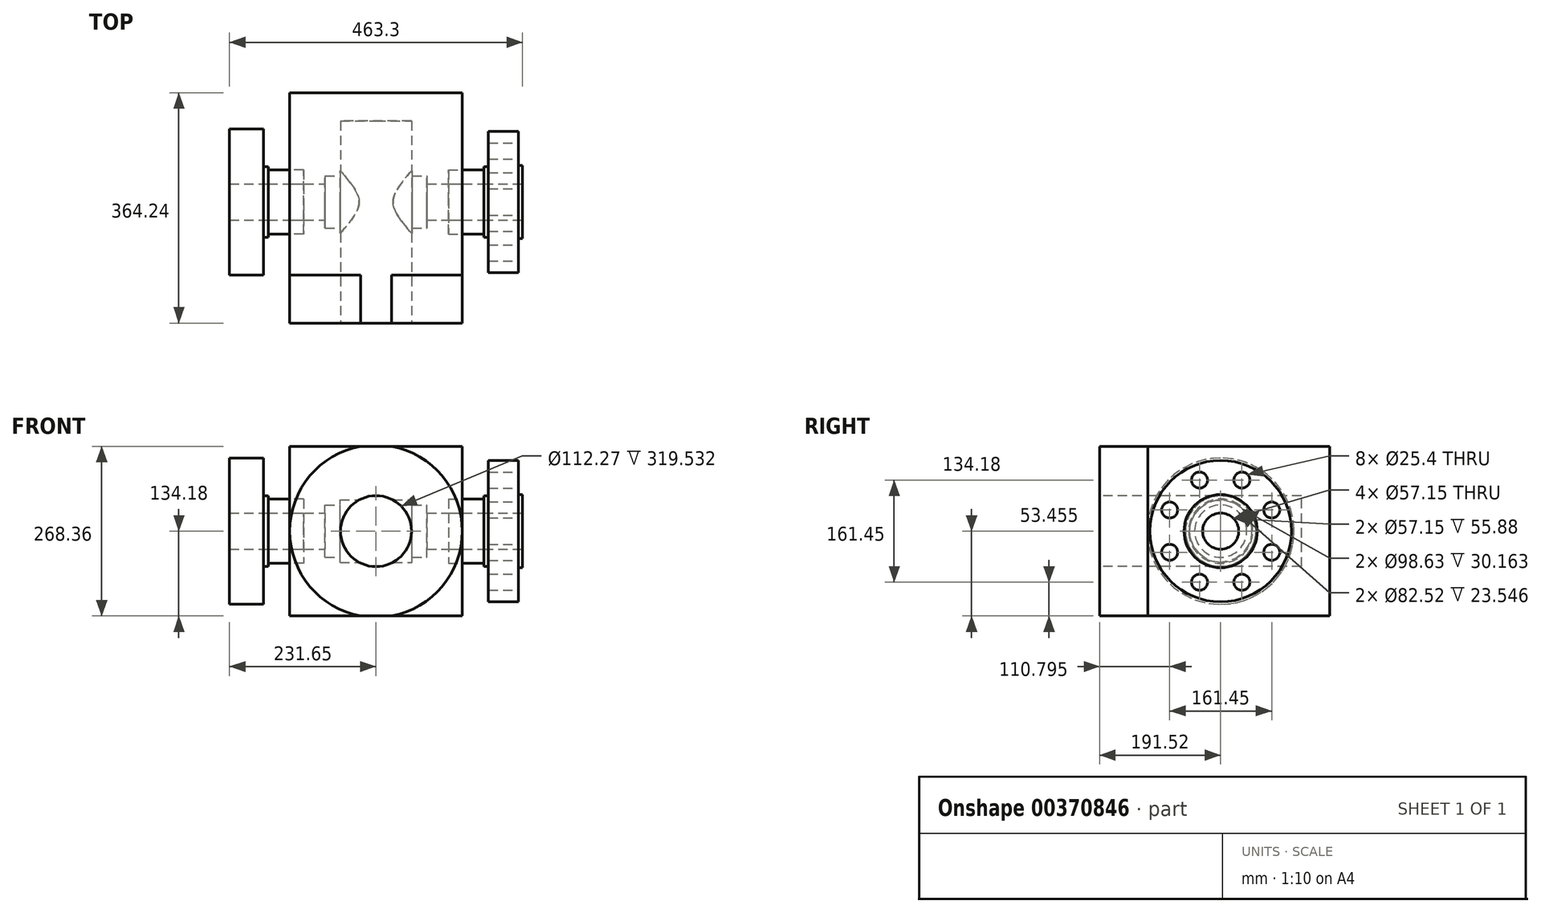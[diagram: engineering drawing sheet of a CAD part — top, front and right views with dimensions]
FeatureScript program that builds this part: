
annotation { "Feature Type Name" : "Feature", "Feature Type Description" : "" }
export const myFeature = defineFeature(function(context is Context, id is Id, definition is map)
    precondition{}
    {
        {
            var Q0;
            Q0=qCreatedBy(makeId("Front.planeOp"),FACE);
            var sketch = newSketch(context, id + "F0", { "sketchPlane" : qUnion([Q0])});
            skLineSegment(sketch, "E0.bottom", {"start": v(-136.4, -134.18) * mm, "end": v(136.4, -134.18) * mm});
            skLineSegment(sketch, "E0.top", {"start": v(-136.4, 134.18) * mm, "end": v(136.4, 134.18) * mm});
            skLineSegment(sketch, "E0.left", {"start": v(-136.4, -134.18) * mm, "end": v(-136.4, 134.18) * mm});
            skLineSegment(sketch, "E0.right", {"start": v(136.4, -134.18) * mm, "end": v(136.4, 134.18) * mm});
            skPoint(sketch, "E0.middle", {"position": v(0, 0) * mm});
            skSolve(sketch);
        }
        {
            var Q0;
            Q0=qSketchRegion(id+"F0",true);
            extrude(context, id + "F1", {"entities" : qUnion([Q0]), "depth" : 191.52 * mm});
        }
        {
            var Q0;
            Q0=makeQuery(id+"F1.opExtrude","CAP_FACE",FACE,{"disambiguationData":[OSD([sQuery(id+"F0.wireOp",EDGE,"E0.bottom"),sQuery(id+"F0.wireOp",EDGE,"E0.top"),sQuery(id+"F0.wireOp",EDGE,"E0.left"),sQuery(id+"F0.wireOp",EDGE,"E0.right")])],"isStart":true});
            extrude(context, id + "F2", {"entities" : qUnion([Q0]), "operationType" : NewBodyOperationType.ADD, "depth" : 172.72 * mm});
        }
        {
            var Q0;
            Q0=qCreatedBy(makeId("Right.planeOp"),FACE);
            cPlane(context, id + "F3", {"entities" : qUnion([Q0]), "cplaneType" : CPlaneType.OFFSET, "offset" : 231.65 * mm, "width" : 152.4 * mm, "height" : 152.4 * mm});
        }
        {
            var Q0;
            Q0=qCreatedBy(id+"F3.planeOp",FACE);
            var sketch = newSketch(context, id + "F4", { "sketchPlane" : qUnion([Q0])});
            skCircle(sketch, "E1", {"center": v(0, 0) * mm, "radius": 115.82 * mm});
            skSolve(sketch);
        }
        {
            var Q0;
            Q0=makeQuery(id+"F4.imprint","IMPRINT",FACE,{"disambiguationData":[TD([[makeQuery(id+"F4.imprint","IMPRINT",EDGE,{"derivedFrom":sQuery(id+"F4.wireOp",EDGE,"E1")}),1.0]])]});
            var Q1;
            Q1=qConstructionFilter(qBodyType(qCreatedBy(id+"F4",EDGE),BodyType.WIRE),ConstructionObject.NO);
            extrude(context, id + "F5", {"entities" : qUnion([Q0]), "surfaceEntities" : qUnion([Q1]), "oppositeDirection" : true, "depth" : 61.2 * mm});
        }
        {
            var Q0;
            Q0=makeQuery(id+"F5.opExtrude","CAP_FACE",FACE,{"disambiguationData":[OSD([sQuery(id+"F4.wireOp",EDGE,"E1")])],"isStart":false});
            var sketch = newSketch(context, id + "F6", { "sketchPlane" : qUnion([Q0])});
            skCircle(sketch, "E2", {"center": v(0, 0) * mm, "radius": 50.8 * mm});
            skSolve(sketch);
        }
        {
            var Q0;
            Q0=qSketchRegion(id+"F6",true);
            extrude(context, id + "F7", {"entities" : qUnion([Q0]), "depth" : 55.88 * mm});
        }
        {
            var Q0;
            Q0=qCreatedBy(makeId("Right.planeOp"),FACE);
            var sketch = newSketch(context, id + "F8", { "sketchPlane" : qUnion([Q0])});
            skLineSegment(sketch, "E3", {"start": v(0, 0) * mm, "end": v(0, 210.58) * mm});
            skSolve(sketch);
        }
        {
            var Q0;
            Q0=makeQuery(id+"F7.opExtrude","SWEPT_BODY",BODY,{"disambiguationData":[OSD([sQuery(id+"F6.wireOp",EDGE,"E2")])]});
            var Q1;
            Q1=makeQuery(id+"F5.opExtrude","SWEPT_BODY",BODY,{"disambiguationData":[OSD([sQuery(id+"F4.wireOp",EDGE,"E1")])]});
            var Q2;
            Q2=sQuery(id+"F8.wireOp",EDGE,"E3");
            circularPattern(context, id + "F9", {"entities" : qUnion([Q0, Q1]), "axis" : qUnion([Q2]), "angle" : 360 * degree, "instanceCount" : 2, "equalSpace" : true});
        }
        {
            var Q0;
            Q0=makeQuery(id+"F5.opExtrude","CAP_FACE",FACE,{"disambiguationData":[OSD([sQuery(id+"F4.wireOp",EDGE,"E1")])],"isStart":true});
            var sketch = newSketch(context, id + "F10", { "sketchPlane" : qUnion([Q0])});
            skCircle(sketch, "E4", {"center": v(0, 0) * mm, "radius": 28.57 * mm});
            skSolve(sketch);
        }
        {
            var Q0;
            Q0=qSketchRegion(id+"F10",true);
            extrude(context, id + "F11", {"entities" : qUnion([Q0]), "operationType" : NewBodyOperationType.REMOVE, "oppositeDirection" : true, "depth" : 701.04 * mm});
        }
        {
            var Q0;
            Q0=makeQuery(id+"F1.opExtrude","CAP_FACE",FACE,{"disambiguationData":[OSD([sQuery(id+"F0.wireOp",EDGE,"E0.bottom"),sQuery(id+"F0.wireOp",EDGE,"E0.top"),sQuery(id+"F0.wireOp",EDGE,"E0.left"),sQuery(id+"F0.wireOp",EDGE,"E0.right")])],"isStart":false});
            var sketch = newSketch(context, id + "F12", { "sketchPlane" : qUnion([Q0])});
            skCircle(sketch, "E5", {"center": v(0, 0) * mm, "radius": 56.13 * mm});
            skSolve(sketch);
        }
        {
            var Q0;
            Q0=qSketchRegion(id+"F12",true);
            extrude(context, id + "F13", {"entities" : qUnion([Q0]), "operationType" : NewBodyOperationType.REMOVE, "oppositeDirection" : true, "depth" : 319.53 * mm});
        }
        {
            var Q0;
            Q0=makeQuery(id+"F1.opExtrude","CAP_FACE",FACE,{"disambiguationData":[OSD([sQuery(id+"F0.wireOp",EDGE,"E0.bottom"),sQuery(id+"F0.wireOp",EDGE,"E0.top"),sQuery(id+"F0.wireOp",EDGE,"E0.left"),sQuery(id+"F0.wireOp",EDGE,"E0.right")])],"isStart":false});
            var sketch = newSketch(context, id + "F14", { "sketchPlane" : qUnion([Q0])});
            skCircle(sketch, "E6", {"center": v(0, 0) * mm, "radius": 136.4 * mm});
            skSolve(sketch);
        }
        {
            var Q0;
            {var subQ0=sQuery(id+"F14.wireOp",EDGE,"E6");var subQ1=makeQuery(id+"F1.opExtrude","CAP_EDGE",EDGE,{"disambiguationData":[OSD([sQuery(id+"F0.wireOp",EDGE,"E0.top")])],"isStart":false});var subQ2=makeQuery(id+"F14.imprint","INTERSECT",VERTEX,{"disambiguationData":[OD(1.0)],"derivedFrom":[subQ1,subQ0]});Q0=makeQuery(id+"F14.imprint","IMPRINT",FACE,{"disambiguationData":[TD([[makeQuery(id+"F14.imprint","IMPRINT",EDGE,{"disambiguationData":[TD([[subQ2,-1.0]])],"derivedFrom":subQ0}),-1.0]])]});}
            var Q1;
            {var subQ0=sQuery(id+"F14.wireOp",EDGE,"E6");var subQ1=makeQuery(id+"F1.opExtrude","CAP_EDGE",EDGE,{"disambiguationData":[OSD([sQuery(id+"F0.wireOp",EDGE,"E0.top")])],"isStart":false});var subQ2=makeQuery(id+"F14.imprint","INTERSECT",VERTEX,{"disambiguationData":[OD(0.0)],"derivedFrom":[subQ1,subQ0]});Q1=makeQuery(id+"F14.imprint","IMPRINT",FACE,{"disambiguationData":[TD([[makeQuery(id+"F14.imprint","IMPRINT",EDGE,{"disambiguationData":[TD([[subQ2,1.0]])],"derivedFrom":subQ0}),-1.0]])]});}
            var Q2;
            {var subQ0=sQuery(id+"F14.wireOp",EDGE,"E6");var subQ1=makeQuery(id+"F1.opExtrude","CAP_EDGE",EDGE,{"disambiguationData":[OSD([sQuery(id+"F0.wireOp",EDGE,"E0.right")])],"isStart":false});var subQ2=makeQuery(id+"F14.imprint","INTERSECT",VERTEX,{"derivedFrom":[subQ1,subQ0]});Q2=makeQuery(id+"F14.imprint","IMPRINT",FACE,{"disambiguationData":[TD([[makeQuery(id+"F14.imprint","IMPRINT",EDGE,{"disambiguationData":[TD([[subQ2,1.0]])],"derivedFrom":subQ0}),-1.0]])]});}
            var Q3;
            {var subQ0=sQuery(id+"F14.wireOp",EDGE,"E6");var subQ1=makeQuery(id+"F1.opExtrude","CAP_EDGE",EDGE,{"disambiguationData":[OSD([sQuery(id+"F0.wireOp",EDGE,"E0.left")])],"isStart":false});var subQ2=makeQuery(id+"F14.imprint","INTERSECT",VERTEX,{"derivedFrom":[subQ1,subQ0]});Q3=makeQuery(id+"F14.imprint","IMPRINT",FACE,{"disambiguationData":[TD([[makeQuery(id+"F14.imprint","IMPRINT",EDGE,{"disambiguationData":[TD([[subQ2,-1.0]])],"derivedFrom":subQ0}),-1.0]])]});}
            extrude(context, id + "F15", {"entities" : qUnion([Q0, Q1, Q2, Q3]), "operationType" : NewBodyOperationType.REMOVE, "oppositeDirection" : true, "depth" : 76.2 * mm});
        }
        {
            var Q0;
            Q0=makeQuery(id+"F5.opExtrude","CAP_FACE",FACE,{"disambiguationData":[OSD([sQuery(id+"F4.wireOp",EDGE,"E1")])],"isStart":true});
            var sketch = newSketch(context, id + "F16", { "sketchPlane" : qUnion([Q0])});
            skCircle(sketch, "E7", {"center": v(0, 0) * mm, "radius": 111.89 * mm});
            skSolve(sketch);
        }
        {
            var Q0;
            Q0=makeQuery(id+"F16.imprint","IMPRINT",FACE,{"disambiguationData":[TD([[makeQuery(id+"F16.imprint","IMPRINT",EDGE,{"derivedFrom":sQuery(id+"F16.wireOp",EDGE,"E7")}),-1.0]])]});
            var Q1;
            Q1=sQuery(id+"F16.wireOp",EDGE,"E7");
            extrude(context, id + "F17", {"entities" : qUnion([Q0]), "operationType" : NewBodyOperationType.REMOVE, "surfaceEntities" : qUnion([Q1]), "oppositeDirection" : true, "depth" : 63.5 * mm});
        }
        {
            var Q0;
            Q0=makeQuery(id+"F5.opExtrude","CAP_FACE",FACE,{"disambiguationData":[OSD([sQuery(id+"F4.wireOp",EDGE,"E1")])],"isStart":true});
            var sketch = newSketch(context, id + "F18", { "sketchPlane" : qUnion([Q0])});
            skLineSegment(sketch, "E8", {"start": v(0, 0) * mm, "end": v(0, 90.21) * mm});
            skLineSegment(sketch, "E9", {"start": v(0, 0) * mm, "end": v(-33.44, 80.72) * mm});
            skCircle(sketch, "E10", {"center": v(-33.44, 80.72) * mm, "radius": 12.7 * mm});
            skCircle(sketch, "E11.1.0", {"center": v(-80.72, 33.44) * mm, "radius": 12.7 * mm});
            skCircle(sketch, "E11.2.0", {"center": v(-80.72, -33.44) * mm, "radius": 12.7 * mm});
            skCircle(sketch, "E11.3.0", {"center": v(-33.44, -80.72) * mm, "radius": 12.7 * mm});
            skCircle(sketch, "E11.4.0", {"center": v(33.44, -80.72) * mm, "radius": 12.7 * mm});
            skCircle(sketch, "E11.5.0", {"center": v(80.72, -33.44) * mm, "radius": 12.7 * mm});
            skCircle(sketch, "E11.6.0", {"center": v(80.72, 33.44) * mm, "radius": 12.7 * mm});
            skCircle(sketch, "E11.7.0", {"center": v(33.44, 80.72) * mm, "radius": 12.7 * mm});
            skPoint(sketch, "E11.center", {"position": v(0, 0) * mm});
            skSolve(sketch);
        }
        {
            var Q0;
            Q0 = qSketchRegion(id + "F18", true);
            extrude(context, id + "F19", {"entities" : qUnion([Q0]), "operationType" : NewBodyOperationType.REMOVE, "oppositeDirection" : true, "depth" : 90.68 * mm});
        }
        {
            var Q0;
            Q0=makeQuery(id+"F5.opExtrude","CAP_FACE",FACE,{"disambiguationData":[OSD([sQuery(id+"F4.wireOp",EDGE,"E1")])],"isStart":true});
            var sketch = newSketch(context, id + "F20", { "sketchPlane" : qUnion([Q0])});
            skCircle(sketch, "E12", {"center": v(0, 0) * mm, "radius": 57.91 * mm});
            skSolve(sketch);
        }
        {
            var Q0;
            Q0=makeQuery(id+"F20.imprint","IMPRINT",FACE,{"disambiguationData":[TD([[makeQuery(id+"F20.imprint","IMPRINT",EDGE,{"derivedFrom":makeQuery(id+"F11.boolean.opBoolean","COPY",EDGE,{"derivedFrom":makeQuery(id+"F11.opExtrude","CAP_EDGE",EDGE,{"disambiguationData":[OSD([sQuery(id+"F10.wireOp",EDGE,"E4")])],"isStart":true})})}),1.0]])]});
            var Q1;
            Q1=makeQuery(id+"F20.imprint","IMPRINT",FACE,{"disambiguationData":[TD([[makeQuery(id+"F20.imprint","IMPRINT",EDGE,{"derivedFrom":sQuery(id+"F20.wireOp",EDGE,"E12")}),-1.0]])]});
            extrude(context, id + "F21", {"entities" : qUnion([Q0, Q1]), "operationType" : NewBodyOperationType.REMOVE, "oppositeDirection" : true, "depth" : 6.35 * mm});
        }
        {
            var Q0;
            Q0=makeQuery(id+"F21.boolean.opBoolean","COPY",EDGE,{"derivedFrom":makeQuery(id+"F21.opExtrude","CAP_EDGE",EDGE,{"disambiguationData":[OSD([sQuery(id+"F20.wireOp",EDGE,"E12")])],"isStart":false})});
            fillet(context, id + "F22", {"entities" : qUnion([Q0]), "radius" : 3.05 * mm, "tangentPropagation" : true, "allowEdgeOverflow" : false});
        }
        {
            var Q0;
            Q0=qCreatedBy(makeId("Top.planeOp"),FACE);
            var sketch = newSketch(context, id + "F23", { "sketchPlane" : qUnion([Q0])});
            skLineSegment(sketch, "E13", {"start": v(0, 0) * mm, "end": v(326.08, 0) * mm});
            skLineSegment(sketch, "E14", {"start": v(80.52, -26.16) * mm, "end": v(329.57, -26.16) * mm});
            skLineSegment(sketch, "E15", {"start": v(34.2, -49.31) * mm, "end": v(56.97, -49.31) * mm});
            skLineSegment(sketch, "E16", {"start": v(56.97, -49.31) * mm, "end": v(56.97, -41.26) * mm});
            skLineSegment(sketch, "E17", {"start": v(56.97, -41.26) * mm, "end": v(80.52, -41.26) * mm});
            skLineSegment(sketch, "E18", {"start": v(80.52, -41.26) * mm, "end": v(80.52, -26.1) * mm});
            skLineSegment(sketch, "E19", {"start": v(177.8, -118.96) * mm, "end": v(177.8, -55.63) * mm});
            skLineSegment(sketch, "E20", {"start": v(177.8, -55.63) * mm, "end": v(155.9, -55.63) * mm});
            skLineSegment(sketch, "E21", {"start": v(155.9, -55.63) * mm, "end": v(155.9, -118.54) * mm});
            skLineSegment(sketch, "E22", {"start": v(155.9, -118.54) * mm, "end": v(177.8, -118.96) * mm});
            skLineSegment(sketch, "E23.MirrorCS", {"start": v(-80.52, -41.26) * mm, "end": v(-80.52, -26.1) * mm});
            skLineSegment(sketch, "E24.MirrorCS", {"start": v(-56.97, -49.31) * mm, "end": v(-56.97, -41.26) * mm});
            skLineSegment(sketch, "E25.MirrorCS", {"start": v(-34.2, -49.31) * mm, "end": v(-56.97, -49.31) * mm});
            skLineSegment(sketch, "E26.MirrorCS", {"start": v(-56.97, -41.26) * mm, "end": v(-80.52, -41.26) * mm});
            skLineSegment(sketch, "E27.MirrorCS", {"start": v(-80.52, -26.16) * mm, "end": v(-329.57, -26.16) * mm});
            skLineSegment(sketch, "E28.MirrorCS", {"start": v(-155.9, -118.54) * mm, "end": v(-177.8, -118.96) * mm});
            skLineSegment(sketch, "E29.MirrorCS", {"start": v(-155.9, -55.63) * mm, "end": v(-155.9, -118.54) * mm});
            skLineSegment(sketch, "E30.MirrorCS", {"start": v(-177.8, -55.63) * mm, "end": v(-155.9, -55.63) * mm});
            skLineSegment(sketch, "E31.MirrorCS", {"start": v(-177.8, -118.96) * mm, "end": v(-177.8, -55.63) * mm});
            skLineSegment(sketch, "E32.MirrorCS", {"start": v(0, 0) * mm, "end": v(-326.08, 0) * mm});
            skLineSegment(sketch, "E33", {"start": v(34.2, -49.31) * mm, "end": v(-34.2, -49.31) * mm});
            skLineSegment(sketch, "E34", {"start": v(-329.57, -26.16) * mm, "end": v(-326.08, 0) * mm});
            skLineSegment(sketch, "E35", {"start": v(329.57, -26.16) * mm, "end": v(326.08, 0) * mm});
            skSolve(sketch);
        }
        {
            var Q0;
            Q0 = qSketchRegion(id + "F23", true);
            var Q1;
            Q1=sQuery(id+"F23.wireOp",EDGE,"E13");
            revolve(context, id + "F24", {"operationType" : NewBodyOperationType.REMOVE, "entities" : qUnion([Q0]), "axis" : qUnion([Q1]), "revolveType" : RevolveType.FULL, "oppositeDirection" : true});
        }
    });
